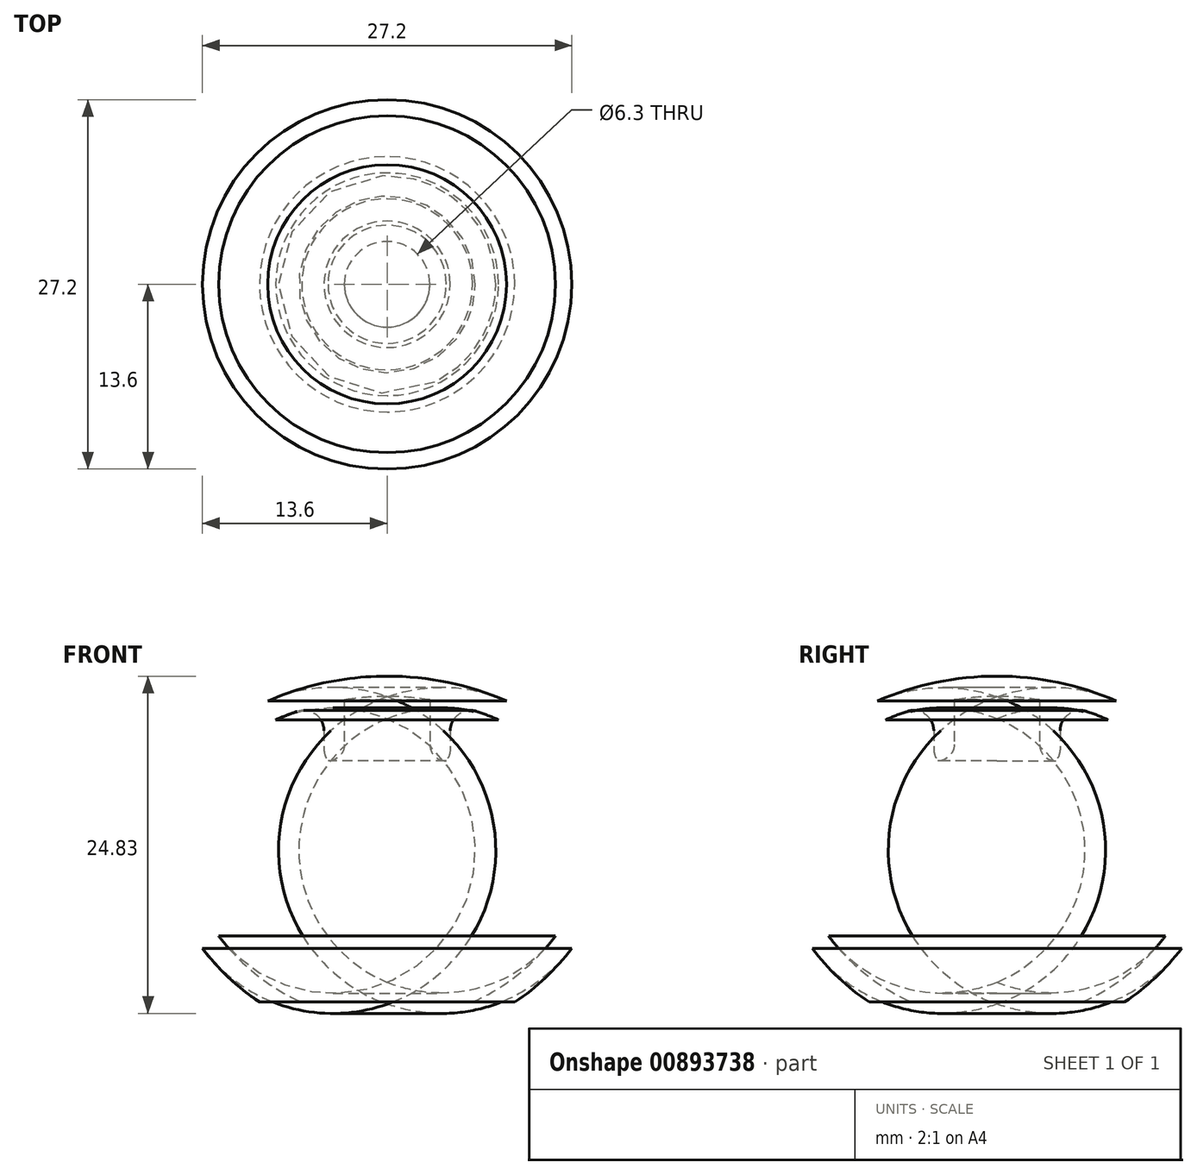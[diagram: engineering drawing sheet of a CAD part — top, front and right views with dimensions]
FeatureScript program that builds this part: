
annotation { "Feature Type Name" : "Feature", "Feature Type Description" : "" }
export const myFeature = defineFeature(function(context is Context, id is Id, definition is map)
    precondition{}
    {
        {
            var Q0;
            Q0=qCreatedBy(makeId("Front.planeOp"),FACE);
            var sketch = newSketch(context, id + "F0", { "sketchPlane" : qUnion([Q0])});
            skLineSegment(sketch, "E0", {"start": v(-4.65, 21.97) * mm, "end": v(-4.65, 17.76) * mm});
            skLineSegment(sketch, "E1", {"start": v(-4.65, 17.76) * mm, "end": v(-3.15, 17.76) * mm});
            skLineSegment(sketch, "E2", {"start": v(-3.15, 17.76) * mm, "end": v(-3.15, 22.26) * mm});
            skLineSegment(sketch, "E3", {"start": v(0, 22.5) * mm, "end": v(0, 24) * mm});
            skLineSegment(sketch, "E4", {"start": v(0, 22.5) * mm, "end": v(-16, 22.5) * mm, "construction": true});
            skArc(sketch, "E5.0", {"start": v(-13.6, 3.97) * mm, "mid": v(-11.67, 1.8) * mm, "end": v(-9.4, 0) * mm});
            skArc(sketch, "E5.1", {"start": v(-8.8, 22.16) * mm, "mid": v(-15.6, 14.23) * mm, "end": v(-13.6, 3.97) * mm});
            skArc(sketch, "E5.2", {"start": v(0, 24) * mm, "mid": v(-4.5, 23.54) * mm, "end": v(-8.8, 22.16) * mm});
            skLineSegment(sketch, "E6", {"start": v(-16, 22.5) * mm, "end": v(-16, 0) * mm, "construction": true});
            skArc(sketch, "E7.0", {"start": v(-12.4, 4.87) * mm, "mid": v(-9.66, 2.04) * mm, "end": v(-6.3, 0) * mm});
            skArc(sketch, "E7.1", {"start": v(-8.2, 20.79) * mm, "mid": v(-14.15, 13.84) * mm, "end": v(-12.4, 4.87) * mm});
            skArc(sketch, "E7.2", {"start": v(0, 22.5) * mm, "mid": v(-4.19, 22.07) * mm, "end": v(-8.2, 20.79) * mm});
            skLineSegment(sketch, "E8", {"start": v(-9.4, 0) * mm, "end": v(-6.3, 0) * mm});
            skLineSegment(sketch, "E9", {"start": v(-6.3, 0) * mm, "end": v(6.48, 28.76) * mm, "construction": true});
            skLineSegment(sketch, "E10", {"start": v(-12.4, 4.87) * mm, "end": v(14.7, 25.19) * mm, "construction": true});
            skLineSegment(sketch, "E11", {"start": v(-8.2, 20.79) * mm, "end": v(7.33, -14.79) * mm, "construction": true});
            skSolve(sketch);
        }
        {
            var Q0;
            Q0=qSketchRegion(id+"F0",true);
            var Q1;
            Q1=sQuery(id+"F0.wireOp",EDGE,"E3");
            revolve(context, id + "F1", {"surfaceOperationType" : NewSurfaceOperationType.NEW, "entities" : qUnion([Q0]), "axis" : qUnion([Q1]), "revolveType" : RevolveType.FULL});
        }
        {
            var Q0;
            Q0=makeQuery(id+"F1.opRevolve","SWEPT_EDGE",EDGE,{"disambiguationData":[OSD([sQuery(id+"F0.wireOp",EDGE,"E1"),sQuery(id+"F0.wireOp",EDGE,"E2")])]});
            fillet(context, id + "F2", {"entities" : qUnion([Q0]), "radius" : 1.2 * mm, "tangentPropagation" : true, "allowEdgeOverflow" : false});
        }
        {
            var Q0;
            Q0=makeQuery(id+"F1.opRevolve","SWEPT_EDGE",EDGE,{"disambiguationData":[OSD([sQuery(id+"F0.wireOp",EDGE,"E0"),sQuery(id+"F0.wireOp",EDGE,"jIFgC7Ky-ozUU-IBoF-aXzB-pM7MHLiFA26t")])]});
            fillet(context, id + "F3", {"entities" : qUnion([Q0]), "radius" : 1.5 * mm, "tangentPropagation" : true, "allowEdgeOverflow" : false});
        }
    });
